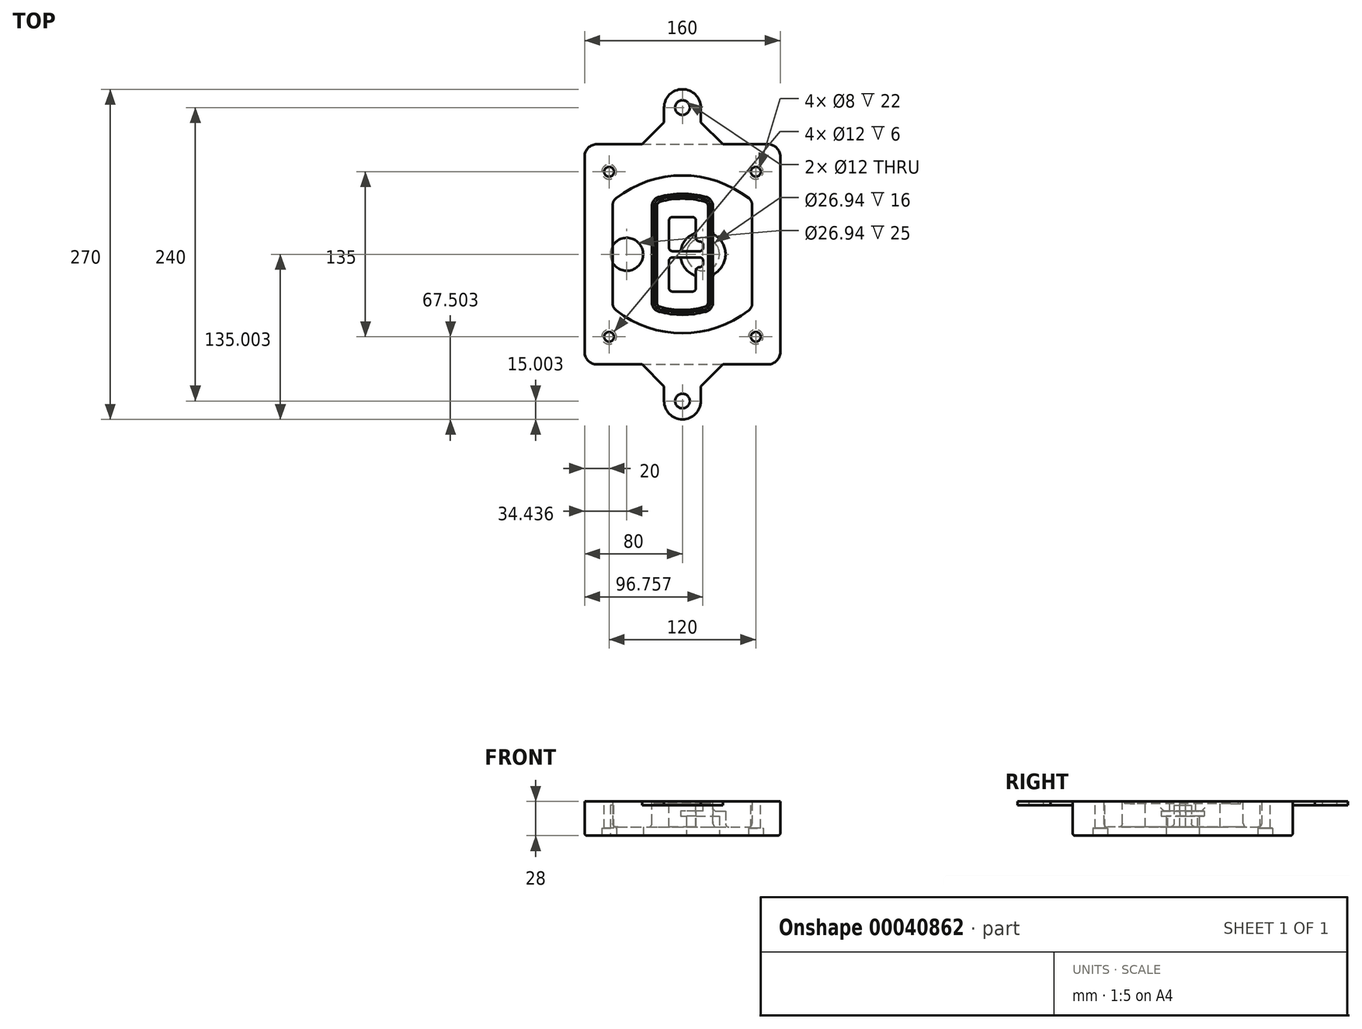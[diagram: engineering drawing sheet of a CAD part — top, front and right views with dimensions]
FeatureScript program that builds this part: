
annotation { "Feature Type Name" : "Feature", "Feature Type Description" : "" }
export const myFeature = defineFeature(function(context is Context, id is Id, definition is map)
    precondition{}
    {
        {
            var Q0;
            Q0=qCreatedBy(makeId("Top.planeOp"),FACE);
            var sketch = newSketch(context, id + "F0", { "sketchPlane" : qUnion([Q0])});
            skPoint(sketch, "E0.rect.middle", {"position": v(0, 0) * mm});
            skLineSegment(sketch, "E1.bottom", {"start": v(24.05, 28.38) * mm, "end": v(164.05, 28.38) * mm});
            skLineSegment(sketch, "E1.top", {"start": v(24.05, 208.38) * mm, "end": v(164.05, 208.38) * mm});
            skLineSegment(sketch, "E1.left", {"start": v(14.05, 38.38) * mm, "end": v(14.05, 198.38) * mm});
            skLineSegment(sketch, "E1.right", {"start": v(174.05, 38.38) * mm, "end": v(174.05, 198.38) * mm});
            skLineSegment(sketch, "E2", {"start": v(14.05, 208.38) * mm, "end": v(174.05, 28.38) * mm, "construction": true});
            skLineSegment(sketch, "E3", {"start": v(174.05, 208.38) * mm, "end": v(14.05, 28.38) * mm, "construction": true});
            skCircle(sketch, "E4", {"center": v(34.05, 185.88) * mm, "radius": 4 * mm});
            skCircle(sketch, "E5", {"center": v(154.05, 185.88) * mm, "radius": 4 * mm});
            skCircle(sketch, "E6", {"center": v(154.05, 50.88) * mm, "radius": 4 * mm});
            skCircle(sketch, "E7", {"center": v(34.05, 50.88) * mm, "radius": 4 * mm});
            skLineSegment(sketch, "E8", {"start": v(34.05, 185.88) * mm, "end": v(154.05, 185.88) * mm, "construction": true});
            skLineSegment(sketch, "E9", {"start": v(154.05, 185.88) * mm, "end": v(154.05, 50.88) * mm, "construction": true});
            skLineSegment(sketch, "E10", {"start": v(154.05, 50.88) * mm, "end": v(34.05, 50.88) * mm, "construction": true});
            skLineSegment(sketch, "E11", {"start": v(34.05, 50.88) * mm, "end": v(34.05, 185.88) * mm, "construction": true});
            skLineSegment(sketch, "E12", {"start": v(34.05, 158.68) * mm, "end": v(34.05, 78.09) * mm});
            skLineSegment(sketch, "E13", {"start": v(154.05, 158.68) * mm, "end": v(154.05, 78.09) * mm});
            skArc(sketch, "E14", {"start": v(150.2, 166.56) * mm, "mid": v(94.05, 185.88) * mm, "end": v(37.9, 166.56) * mm});
            skArc(sketch, "E15", {"start": v(37.9, 70.2) * mm, "mid": v(94.05, 50.88) * mm, "end": v(150.2, 70.2) * mm});
            skLineSegment(sketch, "E16", {"start": v(34.05, 118.38) * mm, "end": v(154.05, 118.38) * mm, "construction": true});
            skPoint(sketch, "E17.visualSharp", {"position": v(34.05, 73.38) * mm});
            skArc(sketch, "E17.filletArc", {"start": v(34.05, 78.09) * mm, "mid": v(35.06, 73.7) * mm, "end": v(37.9, 70.2) * mm});
            skPoint(sketch, "E18.visualSharp", {"position": v(34.05, 163.38) * mm});
            skArc(sketch, "E18.filletArc", {"start": v(37.9, 166.56) * mm, "mid": v(35.06, 163.06) * mm, "end": v(34.05, 158.68) * mm});
            skPoint(sketch, "E19.visualSharp", {"position": v(154.05, 163.38) * mm});
            skArc(sketch, "E19.filletArc", {"start": v(154.05, 158.68) * mm, "mid": v(153.04, 163.06) * mm, "end": v(150.2, 166.56) * mm});
            skPoint(sketch, "E20.visualSharp", {"position": v(154.05, 73.38) * mm});
            skArc(sketch, "E20.filletArc", {"start": v(150.2, 70.2) * mm, "mid": v(153.04, 73.7) * mm, "end": v(154.05, 78.09) * mm});
            skPoint(sketch, "E21.visualSharp", {"position": v(14.05, 208.38) * mm});
            skArc(sketch, "E21.filletArc", {"start": v(24.05, 208.38) * mm, "mid": v(16.98, 205.45) * mm, "end": v(14.05, 198.38) * mm});
            skPoint(sketch, "E22.visualSharp", {"position": v(174.05, 208.38) * mm});
            skArc(sketch, "E22.filletArc", {"start": v(174.05, 198.38) * mm, "mid": v(171.12, 205.45) * mm, "end": v(164.05, 208.38) * mm});
            skPoint(sketch, "E23.visualSharp", {"position": v(174.05, 28.38) * mm});
            skArc(sketch, "E23.filletArc", {"start": v(164.05, 28.38) * mm, "mid": v(171.12, 31.31) * mm, "end": v(174.05, 38.38) * mm});
            skPoint(sketch, "E24.visualSharp", {"position": v(14.05, 28.38) * mm});
            skArc(sketch, "E24.filletArc", {"start": v(14.05, 38.38) * mm, "mid": v(16.98, 31.31) * mm, "end": v(24.05, 28.38) * mm});
            skArc(sketch, "E25.0", {"start": v(151.05, 158.68) * mm, "mid": v(150.34, 161.75) * mm, "end": v(148.36, 164.2) * mm});
            skLineSegment(sketch, "E25.1", {"start": v(151.05, 158.68) * mm, "end": v(151.05, 78.09) * mm});
            skArc(sketch, "E25.2", {"start": v(148.36, 72.57) * mm, "mid": v(150.34, 75.02) * mm, "end": v(151.05, 78.09) * mm});
            skArc(sketch, "E25.3", {"start": v(39.74, 72.57) * mm, "mid": v(94.05, 53.88) * mm, "end": v(148.36, 72.57) * mm});
            skArc(sketch, "E25.4", {"start": v(37.05, 78.09) * mm, "mid": v(37.76, 75.02) * mm, "end": v(39.74, 72.57) * mm});
            skArc(sketch, "E25.5", {"start": v(148.36, 164.2) * mm, "mid": v(94.05, 182.88) * mm, "end": v(39.74, 164.2) * mm});
            skLineSegment(sketch, "E25.6", {"start": v(37.05, 158.68) * mm, "end": v(37.05, 78.09) * mm});
            skArc(sketch, "E25.7", {"start": v(39.74, 164.2) * mm, "mid": v(37.76, 161.75) * mm, "end": v(37.05, 158.68) * mm});
            skArc(sketch, "E26.0", {"start": v(35.43, 169.71) * mm, "mid": v(31.47, 164.82) * mm, "end": v(30.05, 158.68) * mm});
            skArc(sketch, "E26.1", {"start": v(152.67, 169.71) * mm, "mid": v(94.05, 189.88) * mm, "end": v(35.43, 169.71) * mm});
            skArc(sketch, "E26.2", {"start": v(158.05, 158.68) * mm, "mid": v(156.63, 164.82) * mm, "end": v(152.67, 169.71) * mm});
            skLineSegment(sketch, "E26.3", {"start": v(158.05, 158.68) * mm, "end": v(158.05, 78.09) * mm});
            skArc(sketch, "E26.4", {"start": v(152.67, 67.05) * mm, "mid": v(156.63, 71.95) * mm, "end": v(158.05, 78.09) * mm});
            skLineSegment(sketch, "E26.5", {"start": v(30.05, 158.68) * mm, "end": v(30.05, 78.09) * mm});
            skArc(sketch, "E26.6", {"start": v(35.43, 67.05) * mm, "mid": v(94.05, 46.88) * mm, "end": v(152.67, 67.05) * mm});
            skArc(sketch, "E26.7", {"start": v(30.05, 78.09) * mm, "mid": v(31.47, 71.95) * mm, "end": v(35.43, 67.05) * mm});
            skSolve(sketch);
        }
        {
            var Q0;
            Q0=makeQuery(id+"F0.imprint","IMPRINT",FACE,{"disambiguationData":[TD([[makeQuery(id+"F0.imprint","IMPRINT",EDGE,{"derivedFrom":sQuery(id+"F0.wireOp",EDGE,"E1.bottom")}),1.0]])]});
            var Q1;
            Q1=makeQuery(id+"F0.imprint","IMPRINT",FACE,{"disambiguationData":[TD([[makeQuery(id+"F0.imprint","IMPRINT",EDGE,{"derivedFrom":sQuery(id+"F0.wireOp",EDGE,"E12")}),1.0]])]});
            var Q2;
            Q2=makeQuery(id+"F0.imprint","IMPRINT",FACE,{"disambiguationData":[TD([[makeQuery(id+"F0.imprint","IMPRINT",EDGE,{"derivedFrom":sQuery(id+"F0.wireOp",EDGE,"E25.0")}),1.0]])]});
            var Q3;
            Q3=makeQuery(id+"F0.imprint","IMPRINT",FACE,{"disambiguationData":[TD([[makeQuery(id+"F0.imprint","IMPRINT",EDGE,{"derivedFrom":sQuery(id+"F0.wireOp",EDGE,"E12")}),-1.0]])]});
            extrude(context, id + "F1", {"entities" : qUnion([Q0, Q1, Q2, Q3]), "oppositeDirection" : true, "depth" : 25 * mm});
        }
        {
            var Q0;
            Q0=makeQuery(id+"F0.imprint","IMPRINT",FACE,{"disambiguationData":[TD([[makeQuery(id+"F0.imprint","IMPRINT",EDGE,{"derivedFrom":sQuery(id+"F0.wireOp",EDGE,"E12")}),1.0]])]});
            extrude(context, id + "F2", {"entities" : qUnion([Q0]), "operationType" : NewBodyOperationType.ADD, "depth" : 3 * mm});
        }
        {
            var Q0;
            Q0=makeQuery(id+"F0.imprint","IMPRINT",FACE,{"disambiguationData":[TD([[makeQuery(id+"F0.imprint","IMPRINT",EDGE,{"derivedFrom":sQuery(id+"F0.wireOp",EDGE,"E25.0")}),1.0]])]});
            extrude(context, id + "F3", {"entities" : qUnion([Q0]), "operationType" : NewBodyOperationType.REMOVE, "oppositeDirection" : true, "depth" : 18 * mm});
        }
        {
            var Q0;
            Q0=makeQuery(id+"F2.opExtrude","CAP_FACE",FACE,{"disambiguationData":[OSD([sQuery(id+"F0.wireOp",EDGE,"E12"),sQuery(id+"F0.wireOp",EDGE,"E13"),sQuery(id+"F0.wireOp",EDGE,"E14"),sQuery(id+"F0.wireOp",EDGE,"E15"),sQuery(id+"F0.wireOp",EDGE,"E17.filletArc"),sQuery(id+"F0.wireOp",EDGE,"E18.filletArc"),sQuery(id+"F0.wireOp",EDGE,"E19.filletArc"),sQuery(id+"F0.wireOp",EDGE,"E20.filletArc"),sQuery(id+"F0.wireOp",EDGE,"E25.0"),sQuery(id+"F0.wireOp",EDGE,"E25.1"),sQuery(id+"F0.wireOp",EDGE,"E25.2"),sQuery(id+"F0.wireOp",EDGE,"E25.3"),sQuery(id+"F0.wireOp",EDGE,"E25.4"),sQuery(id+"F0.wireOp",EDGE,"E25.5"),sQuery(id+"F0.wireOp",EDGE,"E25.6"),sQuery(id+"F0.wireOp",EDGE,"E25.7")])],"isStart":false});
            var sketch = newSketch(context, id + "F4", { "sketchPlane" : qUnion([Q0])});
            skArc(sketch, "E27.0", {"start": v(74.97, 71.41) * mm, "mid": v(94.05, 68.88) * mm, "end": v(113.13, 71.41) * mm});
            skArc(sketch, "E28.0", {"start": v(113.13, 165.35) * mm, "mid": v(94.05, 167.88) * mm, "end": v(74.97, 165.35) * mm});
            skLineSegment(sketch, "E29", {"start": v(69.05, 157.63) * mm, "end": v(69.05, 79.14) * mm});
            skLineSegment(sketch, "E30", {"start": v(119.05, 157.63) * mm, "end": v(119.05, 79.14) * mm});
            skLineSegment(sketch, "E31", {"start": v(69.05, 163.48) * mm, "end": v(119.05, 163.48) * mm, "construction": true});
            skLineSegment(sketch, "E32", {"start": v(69.05, 73.28) * mm, "end": v(119.05, 73.28) * mm, "construction": true});
            skPoint(sketch, "E33.visualSharp", {"position": v(69.05, 163.48) * mm});
            skArc(sketch, "E33.filletArc", {"start": v(74.97, 165.35) * mm, "mid": v(70.7, 162.5) * mm, "end": v(69.05, 157.63) * mm});
            skPoint(sketch, "E34.visualSharp", {"position": v(119.05, 163.48) * mm});
            skArc(sketch, "E34.filletArc", {"start": v(119.05, 157.63) * mm, "mid": v(117.4, 162.5) * mm, "end": v(113.13, 165.35) * mm});
            skPoint(sketch, "E35.visualSharp", {"position": v(119.05, 73.28) * mm});
            skArc(sketch, "E35.filletArc", {"start": v(113.13, 71.41) * mm, "mid": v(117.4, 74.27) * mm, "end": v(119.05, 79.14) * mm});
            skPoint(sketch, "E36.visualSharp", {"position": v(69.05, 73.28) * mm});
            skArc(sketch, "E36.filletArc", {"start": v(69.05, 79.14) * mm, "mid": v(70.7, 74.27) * mm, "end": v(74.97, 71.41) * mm});
            skArc(sketch, "E37.0", {"start": v(148.36, 164.2) * mm, "mid": v(94.05, 182.88) * mm, "end": v(39.74, 164.2) * mm});
            skArc(sketch, "E37.1", {"start": v(39.74, 164.2) * mm, "mid": v(37.76, 161.75) * mm, "end": v(37.05, 158.68) * mm});
            skLineSegment(sketch, "E37.2", {"start": v(37.05, 158.68) * mm, "end": v(37.05, 78.09) * mm});
            skArc(sketch, "E37.3", {"start": v(37.05, 78.09) * mm, "mid": v(37.76, 75.02) * mm, "end": v(39.74, 72.57) * mm});
            skArc(sketch, "E37.4", {"start": v(39.74, 72.57) * mm, "mid": v(94.05, 53.88) * mm, "end": v(148.36, 72.57) * mm});
            skArc(sketch, "E37.5", {"start": v(148.36, 72.57) * mm, "mid": v(150.34, 75.02) * mm, "end": v(151.05, 78.09) * mm});
            skLineSegment(sketch, "E37.6", {"start": v(151.05, 158.68) * mm, "end": v(151.05, 78.09) * mm});
            skArc(sketch, "E37.7", {"start": v(151.05, 158.68) * mm, "mid": v(150.34, 161.75) * mm, "end": v(148.36, 164.2) * mm});
            skLineSegment(sketch, "E38.0", {"start": v(117.05, 157.63) * mm, "end": v(117.05, 79.14) * mm});
            skArc(sketch, "E38.1", {"start": v(112.61, 73.34) * mm, "mid": v(115.81, 75.49) * mm, "end": v(117.05, 79.14) * mm});
            skArc(sketch, "E38.2", {"start": v(75.49, 73.34) * mm, "mid": v(94.05, 70.88) * mm, "end": v(112.61, 73.34) * mm});
            skArc(sketch, "E38.3", {"start": v(71.05, 79.14) * mm, "mid": v(72.29, 75.49) * mm, "end": v(75.49, 73.34) * mm});
            skLineSegment(sketch, "E38.4", {"start": v(71.05, 157.63) * mm, "end": v(71.05, 79.14) * mm});
            skArc(sketch, "E38.5", {"start": v(117.05, 157.63) * mm, "mid": v(115.81, 161.28) * mm, "end": v(112.61, 163.42) * mm});
            skArc(sketch, "E38.6", {"start": v(75.49, 163.42) * mm, "mid": v(72.29, 161.28) * mm, "end": v(71.05, 157.63) * mm});
            skArc(sketch, "E38.7", {"start": v(112.61, 163.42) * mm, "mid": v(94.05, 165.88) * mm, "end": v(75.49, 163.42) * mm});
            skArc(sketch, "E39.0", {"start": v(115.05, 157.63) * mm, "mid": v(114.23, 160.06) * mm, "end": v(112.1, 161.5) * mm});
            skLineSegment(sketch, "E39.1", {"start": v(115.05, 157.63) * mm, "end": v(115.05, 79.14) * mm});
            skArc(sketch, "E39.2", {"start": v(112.1, 75.27) * mm, "mid": v(114.23, 76.7) * mm, "end": v(115.05, 79.14) * mm});
            skArc(sketch, "E39.3", {"start": v(76, 75.27) * mm, "mid": v(94.05, 72.88) * mm, "end": v(112.1, 75.27) * mm});
            skArc(sketch, "E39.4", {"start": v(73.05, 79.14) * mm, "mid": v(73.87, 76.7) * mm, "end": v(76, 75.27) * mm});
            skArc(sketch, "E39.5", {"start": v(112.1, 161.5) * mm, "mid": v(94.05, 163.88) * mm, "end": v(76, 161.5) * mm});
            skLineSegment(sketch, "E39.6", {"start": v(73.05, 157.63) * mm, "end": v(73.05, 79.14) * mm});
            skArc(sketch, "E39.7", {"start": v(76, 161.5) * mm, "mid": v(73.87, 160.06) * mm, "end": v(73.05, 157.63) * mm});
            skLineSegment(sketch, "E40", {"start": v(69.05, 118.38) * mm, "end": v(119.05, 118.38) * mm, "construction": true});
            skLineSegment(sketch, "E41", {"start": v(83.05, 123.88) * mm, "end": v(83.05, 145.88) * mm});
            skLineSegment(sketch, "E42", {"start": v(86.05, 148.88) * mm, "end": v(102.05, 148.88) * mm});
            skLineSegment(sketch, "E43", {"start": v(105.05, 145.88) * mm, "end": v(105.05, 131.88) * mm});
            skLineSegment(sketch, "E44", {"start": v(108.05, 128.88) * mm, "end": v(108.05, 128.88) * mm});
            skLineSegment(sketch, "E45", {"start": v(111.05, 125.88) * mm, "end": v(111.05, 123.88) * mm});
            skLineSegment(sketch, "E46", {"start": v(108.05, 120.88) * mm, "end": v(86.05, 120.88) * mm});
            skPoint(sketch, "E47.visualSharp", {"position": v(83.05, 148.88) * mm});
            skArc(sketch, "E47.filletArc", {"start": v(86.05, 148.88) * mm, "mid": v(83.93, 148) * mm, "end": v(83.05, 145.88) * mm});
            skPoint(sketch, "E48.visualSharp", {"position": v(105.05, 148.88) * mm});
            skArc(sketch, "E48.filletArc", {"start": v(105.05, 145.88) * mm, "mid": v(104.17, 148) * mm, "end": v(102.05, 148.88) * mm});
            skPoint(sketch, "E49.visualSharp", {"position": v(105.05, 128.88) * mm});
            skArc(sketch, "E49.filletArc", {"start": v(105.05, 131.88) * mm, "mid": v(105.93, 129.76) * mm, "end": v(108.05, 128.88) * mm});
            skPoint(sketch, "E50.visualSharp", {"position": v(111.05, 128.88) * mm});
            skArc(sketch, "E50.filletArc", {"start": v(111.05, 125.88) * mm, "mid": v(110.17, 128) * mm, "end": v(108.05, 128.88) * mm});
            skPoint(sketch, "E51.visualSharp", {"position": v(111.05, 120.88) * mm});
            skArc(sketch, "E51.filletArc", {"start": v(108.05, 120.88) * mm, "mid": v(110.17, 121.76) * mm, "end": v(111.05, 123.88) * mm});
            skPoint(sketch, "E52.visualSharp", {"position": v(83.05, 120.88) * mm});
            skArc(sketch, "E52.filletArc", {"start": v(83.05, 123.88) * mm, "mid": v(83.93, 121.76) * mm, "end": v(86.05, 120.88) * mm});
            skLineSegment(sketch, "E53.0.MirrorCS", {"start": v(108.05, 115.88) * mm, "end": v(86.05, 115.88) * mm});
            skArc(sketch, "E54.0.MirrorCS", {"start": v(83.05, 112.88) * mm, "mid": v(83.93, 115) * mm, "end": v(86.05, 115.88) * mm});
            skLineSegment(sketch, "E55.0.MirrorCS", {"start": v(83.05, 112.88) * mm, "end": v(83.05, 90.88) * mm});
            skArc(sketch, "E56.0.MirrorCS", {"start": v(86.05, 87.88) * mm, "mid": v(83.93, 88.76) * mm, "end": v(83.05, 90.88) * mm});
            skLineSegment(sketch, "E57.0.MirrorCS", {"start": v(86.05, 87.88) * mm, "end": v(102.05, 87.88) * mm});
            skArc(sketch, "E58.0.MirrorCS", {"start": v(105.05, 90.88) * mm, "mid": v(104.17, 88.76) * mm, "end": v(102.05, 87.88) * mm});
            skLineSegment(sketch, "E59.0.MirrorCS", {"start": v(105.05, 90.88) * mm, "end": v(105.05, 104.88) * mm});
            skArc(sketch, "E60.0.MirrorCS", {"start": v(105.05, 104.88) * mm, "mid": v(105.93, 107) * mm, "end": v(108.05, 107.88) * mm});
            skArc(sketch, "E61.0.MirrorCS", {"start": v(111.05, 110.88) * mm, "mid": v(110.17, 108.76) * mm, "end": v(108.05, 107.88) * mm});
            skLineSegment(sketch, "E62.0.MirrorCS", {"start": v(111.05, 110.88) * mm, "end": v(111.05, 112.88) * mm});
            skArc(sketch, "E63.0.MirrorCS", {"start": v(108.05, 115.88) * mm, "mid": v(110.17, 115) * mm, "end": v(111.05, 112.88) * mm});
            skSolve(sketch);
        }
        {
            var Q0;
            Q0=makeQuery(id+"F4.imprint","IMPRINT",FACE,{"disambiguationData":[TD([[makeQuery(id+"F4.imprint","IMPRINT",EDGE,{"derivedFrom":sQuery(id+"F4.wireOp",EDGE,"E27.0")}),1.0]])]});
            var Q1;
            Q1=makeQuery(id+"F4.imprint","IMPRINT",FACE,{"disambiguationData":[TD([[makeQuery(id+"F4.imprint","IMPRINT",EDGE,{"derivedFrom":sQuery(id+"F4.wireOp",EDGE,"E38.0")}),-1.0]])]});
            var Q2;
            Q2=makeQuery(id+"F4.imprint","IMPRINT",FACE,{"disambiguationData":[TD([[makeQuery(id+"F4.imprint","IMPRINT",EDGE,{"derivedFrom":sQuery(id+"F4.wireOp",EDGE,"E39.0")}),1.0]])]});
            extrude(context, id + "F5", {"entities" : qUnion([Q0, Q1, Q2]), "operationType" : NewBodyOperationType.ADD, "endBound" : BoundingType.UP_TO_NEXT, "oppositeDirection" : true, "depth" : 25 * mm});
        }
        {
            var Q0;
            Q0=makeQuery(id+"F4.imprint","IMPRINT",FACE,{"disambiguationData":[TD([[makeQuery(id+"F4.imprint","IMPRINT",EDGE,{"derivedFrom":sQuery(id+"F4.wireOp",EDGE,"E38.0")}),-1.0]])]});
            extrude(context, id + "F6", {"entities" : qUnion([Q0]), "operationType" : NewBodyOperationType.REMOVE, "oppositeDirection" : true, "depth" : 2 * mm});
        }
        {
            var Q0;
            Q0=makeQuery(id+"F1.opExtrude","CAP_FACE",FACE,{"disambiguationData":[OSD([sQuery(id+"F0.wireOp",EDGE,"E1.bottom"),sQuery(id+"F0.wireOp",EDGE,"E1.top"),sQuery(id+"F0.wireOp",EDGE,"E1.left"),sQuery(id+"F0.wireOp",EDGE,"E1.right"),sQuery(id+"F0.wireOp",EDGE,"E4"),sQuery(id+"F0.wireOp",EDGE,"E5"),sQuery(id+"F0.wireOp",EDGE,"E6"),sQuery(id+"F0.wireOp",EDGE,"E7"),sQuery(id+"F0.wireOp",EDGE,"E21.filletArc"),sQuery(id+"F0.wireOp",EDGE,"E22.filletArc"),sQuery(id+"F0.wireOp",EDGE,"E23.filletArc"),sQuery(id+"F0.wireOp",EDGE,"E24.filletArc")])],"isStart":false});
            var sketch = newSketch(context, id + "F7", { "sketchPlane" : qUnion([Q0])});
            skCircle(sketch, "E64", {"center": v(110.8, -118.38) * mm, "radius": 13.47 * mm});
            skCircle(sketch, "E65", {"center": v(48.49, -118.38) * mm, "radius": 13.47 * mm});
            skLineSegment(sketch, "E66", {"start": v(174.05, -118.38) * mm, "end": v(14.05, -118.38) * mm});
            skCircle(sketch, "E67", {"center": v(110.8, -118.38) * mm, "radius": 18.47 * mm});
            skCircle(sketch, "E68", {"center": v(154.05, -185.88) * mm, "radius": 6 * mm});
            skCircle(sketch, "E69", {"center": v(34.05, -185.88) * mm, "radius": 6 * mm});
            skCircle(sketch, "E70", {"center": v(34.05, -50.88) * mm, "radius": 6 * mm});
            skCircle(sketch, "E71", {"center": v(154.05, -50.88) * mm, "radius": 6 * mm});
            skSolve(sketch);
        }
        {
            var Q0;
            {var subQ1=sQuery(id+"F7.wireOp",EDGE,"E66");var subQ4=sQuery(id+"F7.wireOp",EDGE,"E64");var subQ6=makeQuery(id+"F7.imprint","INTERSECT",VERTEX,{"disambiguationData":[OD(0.0)],"derivedFrom":[subQ4,subQ1]});Q0=makeQuery(id+"F7.imprint","IMPRINT",FACE,{"disambiguationData":[TD([[makeQuery(id+"F7.imprint","IMPRINT",EDGE,{"disambiguationData":[TD([[subQ6,-1.0]])],"derivedFrom":subQ4}),-1.0]])]});}
            var Q1;
            {var subQ0=sQuery(id+"F7.wireOp",EDGE,"E66");var subQ1=sQuery(id+"F7.wireOp",EDGE,"E64");var subQ3=makeQuery(id+"F7.imprint","INTERSECT",VERTEX,{"disambiguationData":[OD(0.0)],"derivedFrom":[subQ1,subQ0]});Q1=makeQuery(id+"F7.imprint","IMPRINT",FACE,{"disambiguationData":[TD([[makeQuery(id+"F7.imprint","IMPRINT",EDGE,{"disambiguationData":[TD([[subQ3,-1.0]])],"derivedFrom":subQ1}),1.0]])]});}
            var Q2;
            {var subQ0=sQuery(id+"F7.wireOp",EDGE,"E66");var subQ1=sQuery(id+"F7.wireOp",EDGE,"E64");var subQ3=makeQuery(id+"F7.imprint","INTERSECT",VERTEX,{"disambiguationData":[OD(0.0)],"derivedFrom":[subQ1,subQ0]});Q2=makeQuery(id+"F7.imprint","IMPRINT",FACE,{"disambiguationData":[TD([[makeQuery(id+"F7.imprint","IMPRINT",EDGE,{"disambiguationData":[TD([[subQ3,1.0]])],"derivedFrom":subQ1}),1.0]])]});}
            var Q3;
            {var subQ1=sQuery(id+"F7.wireOp",EDGE,"E66");var subQ4=sQuery(id+"F7.wireOp",EDGE,"E64");var subQ6=makeQuery(id+"F7.imprint","INTERSECT",VERTEX,{"disambiguationData":[OD(0.0)],"derivedFrom":[subQ4,subQ1]});Q3=makeQuery(id+"F7.imprint","IMPRINT",FACE,{"disambiguationData":[TD([[makeQuery(id+"F7.imprint","IMPRINT",EDGE,{"disambiguationData":[TD([[subQ6,1.0]])],"derivedFrom":subQ4}),-1.0]])]});}
            extrude(context, id + "F8", {"entities" : qUnion([Q0, Q1, Q2, Q3]), "operationType" : NewBodyOperationType.ADD, "oppositeDirection" : true, "depth" : 20 * mm});
        }
        {
            var Q0;
            {var subQ0=sQuery(id+"F7.wireOp",EDGE,"E66");var subQ1=sQuery(id+"F7.wireOp",EDGE,"E64");var subQ3=makeQuery(id+"F7.imprint","INTERSECT",VERTEX,{"disambiguationData":[OD(0.0)],"derivedFrom":[subQ1,subQ0]});Q0=makeQuery(id+"F7.imprint","IMPRINT",FACE,{"disambiguationData":[TD([[makeQuery(id+"F7.imprint","IMPRINT",EDGE,{"disambiguationData":[TD([[subQ3,-1.0]])],"derivedFrom":subQ1}),1.0]])]});}
            var Q1;
            {var subQ0=sQuery(id+"F7.wireOp",EDGE,"E66");var subQ1=sQuery(id+"F7.wireOp",EDGE,"E64");var subQ3=makeQuery(id+"F7.imprint","INTERSECT",VERTEX,{"disambiguationData":[OD(0.0)],"derivedFrom":[subQ1,subQ0]});Q1=makeQuery(id+"F7.imprint","IMPRINT",FACE,{"disambiguationData":[TD([[makeQuery(id+"F7.imprint","IMPRINT",EDGE,{"disambiguationData":[TD([[subQ3,1.0]])],"derivedFrom":subQ1}),1.0]])]});}
            extrude(context, id + "F9", {"entities" : qUnion([Q0, Q1]), "operationType" : NewBodyOperationType.REMOVE, "oppositeDirection" : true, "depth" : 16 * mm});
        }
        {
            var Q0;
            {var subQ0=sQuery(id+"F7.wireOp",EDGE,"E66");var subQ1=sQuery(id+"F7.wireOp",EDGE,"E65");var subQ3=makeQuery(id+"F7.imprint","INTERSECT",VERTEX,{"disambiguationData":[OD(0.0)],"derivedFrom":[subQ1,subQ0]});Q0=makeQuery(id+"F7.imprint","IMPRINT",FACE,{"disambiguationData":[TD([[makeQuery(id+"F7.imprint","IMPRINT",EDGE,{"disambiguationData":[TD([[subQ3,-1.0]])],"derivedFrom":subQ1}),1.0]])]});}
            var Q1;
            {var subQ0=sQuery(id+"F7.wireOp",EDGE,"E66");var subQ1=sQuery(id+"F7.wireOp",EDGE,"E65");var subQ3=makeQuery(id+"F7.imprint","INTERSECT",VERTEX,{"disambiguationData":[OD(0.0)],"derivedFrom":[subQ1,subQ0]});Q1=makeQuery(id+"F7.imprint","IMPRINT",FACE,{"disambiguationData":[TD([[makeQuery(id+"F7.imprint","IMPRINT",EDGE,{"disambiguationData":[TD([[subQ3,1.0]])],"derivedFrom":subQ1}),1.0]])]});}
            extrude(context, id + "F10", {"entities" : qUnion([Q0, Q1]), "operationType" : NewBodyOperationType.REMOVE, "oppositeDirection" : true, "depth" : 25 * mm});
        }
        {
            var Q0;
            Q0=makeQuery(id+"F7.imprint","IMPRINT",FACE,{"disambiguationData":[TD([[makeQuery(id+"F7.imprint","IMPRINT",EDGE,{"derivedFrom":sQuery(id+"F7.wireOp",EDGE,"E68")}),1.0]])]});
            var Q1;
            Q1=makeQuery(id+"F7.imprint","IMPRINT",FACE,{"disambiguationData":[TD([[makeQuery(id+"F7.imprint","IMPRINT",EDGE,{"derivedFrom":makeQuery(id+"F1.opExtrude","CAP_EDGE",EDGE,{"disambiguationData":[OSD([sQuery(id+"F0.wireOp",EDGE,"E5")])],"isStart":false})}),-1.0]])]});
            var Q2;
            Q2=makeQuery(id+"F7.imprint","IMPRINT",FACE,{"disambiguationData":[TD([[makeQuery(id+"F7.imprint","IMPRINT",EDGE,{"derivedFrom":sQuery(id+"F7.wireOp",EDGE,"E69")}),1.0]])]});
            var Q3;
            Q3=makeQuery(id+"F7.imprint","IMPRINT",FACE,{"disambiguationData":[TD([[makeQuery(id+"F7.imprint","IMPRINT",EDGE,{"derivedFrom":makeQuery(id+"F1.opExtrude","CAP_EDGE",EDGE,{"disambiguationData":[OSD([sQuery(id+"F0.wireOp",EDGE,"E4")])],"isStart":false})}),-1.0]])]});
            var Q4;
            Q4=makeQuery(id+"F7.imprint","IMPRINT",FACE,{"disambiguationData":[TD([[makeQuery(id+"F7.imprint","IMPRINT",EDGE,{"derivedFrom":sQuery(id+"F7.wireOp",EDGE,"E70")}),1.0]])]});
            var Q5;
            Q5=makeQuery(id+"F7.imprint","IMPRINT",FACE,{"disambiguationData":[TD([[makeQuery(id+"F7.imprint","IMPRINT",EDGE,{"derivedFrom":makeQuery(id+"F1.opExtrude","CAP_EDGE",EDGE,{"disambiguationData":[OSD([sQuery(id+"F0.wireOp",EDGE,"E7")])],"isStart":false})}),-1.0]])]});
            var Q6;
            Q6=makeQuery(id+"F7.imprint","IMPRINT",FACE,{"disambiguationData":[TD([[makeQuery(id+"F7.imprint","IMPRINT",EDGE,{"derivedFrom":sQuery(id+"F7.wireOp",EDGE,"E71")}),1.0]])]});
            var Q7;
            Q7=makeQuery(id+"F7.imprint","IMPRINT",FACE,{"disambiguationData":[TD([[makeQuery(id+"F7.imprint","IMPRINT",EDGE,{"derivedFrom":makeQuery(id+"F1.opExtrude","CAP_EDGE",EDGE,{"disambiguationData":[OSD([sQuery(id+"F0.wireOp",EDGE,"E6")])],"isStart":false})}),-1.0]])]});
            extrude(context, id + "F11", {"entities" : qUnion([Q0, Q1, Q2, Q3, Q4, Q5, Q6, Q7]), "operationType" : NewBodyOperationType.REMOVE, "oppositeDirection" : true, "depth" : 6 * mm});
        }
        {
            var Q0;
            Q0=makeQuery(id+"F9.boolean.opBoolean","COPY",FACE,{"derivedFrom":makeQuery(id+"F9.opExtrude","CAP_FACE",FACE,{"disambiguationData":[OSD([sQuery(id+"F7.wireOp",EDGE,"E64")])],"isStart":false})});
            var sketch = newSketch(context, id + "F12", { "sketchPlane" : qUnion([Q0])});
            skArc(sketch, "E72.0", {"start": v(105.05, -100.83) * mm, "mid": v(96.62, -106.56) * mm, "end": v(92.5, -115.88) * mm});
            skArc(sketch, "E72.1", {"start": v(92.5, -120.88) * mm, "mid": v(96.62, -130.2) * mm, "end": v(105.05, -135.93) * mm});
            skLineSegment(sketch, "E73", {"start": v(92.5, -120.88) * mm, "end": v(108.05, -120.88) * mm});
            skLineSegment(sketch, "E74.0", {"start": v(108.05, -115.88) * mm, "end": v(92.5, -115.88) * mm});
            skArc(sketch, "E74.1", {"start": v(108.05, -115.88) * mm, "mid": v(110.17, -115) * mm, "end": v(111.05, -112.88) * mm});
            skLineSegment(sketch, "E74.2", {"start": v(111.05, -110.88) * mm, "end": v(111.05, -112.88) * mm});
            skArc(sketch, "E74.3", {"start": v(111.05, -110.88) * mm, "mid": v(110.17, -108.76) * mm, "end": v(108.05, -107.88) * mm});
            skArc(sketch, "E74.4", {"start": v(105.05, -104.88) * mm, "mid": v(105.93, -107) * mm, "end": v(108.05, -107.88) * mm});
            skLineSegment(sketch, "E74.5", {"start": v(105.05, -100.83) * mm, "end": v(105.05, -104.88) * mm});
            skLineSegment(sketch, "E74.7", {"start": v(108.05, -120.88) * mm, "end": v(92.5, -120.88) * mm});
            skArc(sketch, "E74.8", {"start": v(108.05, -120.88) * mm, "mid": v(110.17, -121.76) * mm, "end": v(111.05, -123.88) * mm});
            skLineSegment(sketch, "E74.9", {"start": v(111.05, -125.88) * mm, "end": v(111.05, -123.88) * mm});
            skArc(sketch, "E74.10", {"start": v(111.05, -125.88) * mm, "mid": v(110.17, -128) * mm, "end": v(108.05, -128.88) * mm});
            skArc(sketch, "E74.11", {"start": v(105.05, -131.88) * mm, "mid": v(105.93, -129.76) * mm, "end": v(108.05, -128.88) * mm});
            skLineSegment(sketch, "E74.12", {"start": v(105.05, -135.93) * mm, "end": v(105.05, -131.88) * mm});
            skPoint(sketch, "E75.orphan", {"position": v(105.05, -145.88) * mm});
            skPoint(sketch, "E76.orphan", {"position": v(86.05, -120.88) * mm});
            skPoint(sketch, "E77.orphan", {"position": v(86.05, -115.88) * mm});
            skPoint(sketch, "E78.orphan", {"position": v(105.05, -90.88) * mm});
            skSolve(sketch);
        }
        {
            var Q0;
            {var subQ7=sQuery(id+"F12.wireOp",EDGE,"E72.0");var subQ14=sQuery(id+"F12.wireOp",EDGE,"E72.1");var subQ16=sQuery(id+"F12.wireOp",EDGE,"E74.1");var subQ18=sQuery(id+"F12.wireOp",EDGE,"E74.8");Q0=qUnion([makeQuery(id+"F12.imprint","IMPRINT",FACE,{"disambiguationData":[TD([[makeQuery(id+"F12.imprint","IMPRINT",EDGE,{"derivedFrom":subQ7}),1.0]])]}),makeQuery(id+"F12.imprint","IMPRINT",FACE,{"disambiguationData":[TD([[makeQuery(id+"F12.imprint","IMPRINT",EDGE,{"derivedFrom":subQ14}),1.0]])]}),makeQuery(id+"F12.imprint","IMPRINT",FACE,{"disambiguationData":[TD([[makeQuery(id+"F12.imprint","IMPRINT",EDGE,{"derivedFrom":subQ16}),1.0]])]}),makeQuery(id+"F12.imprint","IMPRINT",FACE,{"disambiguationData":[TD([[makeQuery(id+"F12.imprint","IMPRINT",EDGE,{"derivedFrom":subQ18}),-1.0]])]})]);}
            var Q1;
            Q1=makeQuery(id+"F5.boolean.opBoolean","SPLIT",FACE,{"disambiguationData":[TD([makeQuery(id+"F5.opExtrude","SWEPT_FACE",FACE,{"disambiguationData":[OSD([sQuery(id+"F4.wireOp",EDGE,"E41")])]})])],"derivedFrom":makeQuery(id+"F3.boolean.opBoolean","COPY",FACE,{"derivedFrom":makeQuery(id+"F3.opExtrude","CAP_FACE",FACE,{"disambiguationData":[OSD([sQuery(id+"F0.wireOp",EDGE,"E25.0"),sQuery(id+"F0.wireOp",EDGE,"E25.1"),sQuery(id+"F0.wireOp",EDGE,"E25.2"),sQuery(id+"F0.wireOp",EDGE,"E25.3"),sQuery(id+"F0.wireOp",EDGE,"E25.4"),sQuery(id+"F0.wireOp",EDGE,"E25.5"),sQuery(id+"F0.wireOp",EDGE,"E25.6"),sQuery(id+"F0.wireOp",EDGE,"E25.7")])],"isStart":false})})});
            extrude(context, id + "F13", {"entities" : qUnion([Q0]), "operationType" : NewBodyOperationType.REMOVE, "endBound" : BoundingType.UP_TO_SURFACE, "endBoundEntityFace" : qUnion([Q1]), "depth" : 25 * mm});
        }
        {
            var Q0;
            Q0=makeQuery(id+"F3.boolean.opBoolean","COPY",EDGE,{"derivedFrom":makeQuery(id+"F3.opExtrude","CAP_EDGE",EDGE,{"disambiguationData":[OSD([sQuery(id+"F0.wireOp",EDGE,"E25.6")])],"isStart":false})});
            var Q1;
            Q1=makeQuery(id+"F8.boolean.opBoolean","INTERSECT",EDGE,{"derivedFrom":[makeQuery(id+"F5.opExtrude","SWEPT_FACE",FACE,{"disambiguationData":[OSD([sQuery(id+"F4.wireOp",EDGE,"E30")])]}),makeQuery(id+"F8.opExtrude","CAP_FACE",FACE,{"disambiguationData":[OSD([sQuery(id+"F7.wireOp",EDGE,"E67")])],"isStart":false})]});
            var Q2;
            Q2=makeQuery(id+"F8.boolean.opBoolean","INTERSECT",EDGE,{"disambiguationData":[OD(1.0)],"derivedFrom":[makeQuery(id+"F5.opExtrude","SWEPT_FACE",FACE,{"disambiguationData":[OSD([sQuery(id+"F4.wireOp",EDGE,"E30")])]}),makeQuery(id+"F8.opExtrude","SWEPT_FACE",FACE,{"disambiguationData":[OSD([sQuery(id+"F7.wireOp",EDGE,"E67")])]})]});
            var Q3;
            {var subQ0=sQuery(id+"F4.wireOp",EDGE,"E30");Q3=makeQuery(id+"F8.boolean.opBoolean","SPLIT",EDGE,{"disambiguationData":[TD([makeQuery(id+"F5.opExtrude","SWEPT_FACE",FACE,{"disambiguationData":[OSD([sQuery(id+"F4.wireOp",EDGE,"E35.filletArc")])]})])],"derivedFrom":makeQuery(id+"F5.opExtrude","CAP_EDGE",EDGE,{"disambiguationData":[OSD([subQ0])],"isStart":false})});}
            var Q4;
            {var subQ0=sQuery(id+"F0.wireOp",EDGE,"E25.7");var subQ1=sQuery(id+"F0.wireOp",EDGE,"E25.1");var subQ2=sQuery(id+"F0.wireOp",EDGE,"E25.6");var subQ3=sQuery(id+"F0.wireOp",EDGE,"E25.5");var subQ4=sQuery(id+"F0.wireOp",EDGE,"E25.4");var subQ5=sQuery(id+"F0.wireOp",EDGE,"E25.0");var subQ6=sQuery(id+"F0.wireOp",EDGE,"E25.2");var subQ7=sQuery(id+"F0.wireOp",EDGE,"E25.3");Q4=makeQuery(id+"F8.boolean.opBoolean","INTERSECT",EDGE,{"derivedFrom":[makeQuery(id+"F5.boolean.opBoolean","SPLIT",FACE,{"disambiguationData":[TD([makeQuery(id+"F2.opExtrude","SWEPT_FACE",FACE,{"disambiguationData":[OSD([subQ5])]})])],"derivedFrom":makeQuery(id+"F3.boolean.opBoolean","COPY",FACE,{"derivedFrom":makeQuery(id+"F3.opExtrude","CAP_FACE",FACE,{"disambiguationData":[OSD([subQ5,subQ1,subQ6,subQ7,subQ4,subQ3,subQ2,subQ0])],"isStart":false})})}),makeQuery(id+"F8.opExtrude","SWEPT_FACE",FACE,{"disambiguationData":[OSD([sQuery(id+"F7.wireOp",EDGE,"E67")])]})]});}
            var Q5;
            Q5=makeQuery(id+"F8.boolean.opBoolean","INTERSECT",EDGE,{"disambiguationData":[OD(0.0)],"derivedFrom":[makeQuery(id+"F5.opExtrude","SWEPT_FACE",FACE,{"disambiguationData":[OSD([sQuery(id+"F4.wireOp",EDGE,"E30")])]}),makeQuery(id+"F8.opExtrude","SWEPT_FACE",FACE,{"disambiguationData":[OSD([sQuery(id+"F7.wireOp",EDGE,"E67")])]})]});
            fillet(context, id + "F14", {"entities" : qUnion([Q0, Q1, Q2, Q3, Q4, Q5]), "radius" : 3 * mm, "tangentPropagation" : true, "allowEdgeOverflow" : false});
        }
        {
            var Q0;
            Q0=makeQuery(id+"F1.opExtrude","CAP_EDGE",EDGE,{"disambiguationData":[OSD([sQuery(id+"F0.wireOp",EDGE,"E1.bottom")])],"isStart":false});
            fillet(context, id + "F15", {"entities" : qUnion([Q0]), "radius" : 2 * mm, "tangentPropagation" : true, "allowEdgeOverflow" : false});
        }
        {
            var Q0;
            {var subQ0=sQuery(id+"F0.wireOp",EDGE,"E1.bottom");var subQ1=sQuery(id+"F0.wireOp",EDGE,"E1.top");var subQ2=sQuery(id+"F0.wireOp",EDGE,"E1.left");var subQ3=sQuery(id+"F0.wireOp",EDGE,"E1.right");var subQ4=sQuery(id+"F0.wireOp",EDGE,"E4");var subQ5=sQuery(id+"F0.wireOp",EDGE,"E5");var subQ6=sQuery(id+"F0.wireOp",EDGE,"E6");var subQ7=sQuery(id+"F0.wireOp",EDGE,"E7");var subQ8=sQuery(id+"F0.wireOp",EDGE,"E21.filletArc");var subQ9=sQuery(id+"F0.wireOp",EDGE,"E22.filletArc");var subQ10=sQuery(id+"F0.wireOp",EDGE,"E23.filletArc");var subQ11=sQuery(id+"F0.wireOp",EDGE,"E24.filletArc");Q0=makeQuery(id+"F2.boolean.opBoolean","SPLIT",FACE,{"disambiguationData":[TD([makeQuery(id+"F1.opExtrude","SWEPT_FACE",FACE,{"disambiguationData":[OSD([subQ0])]})])],"derivedFrom":makeQuery(id+"F1.opExtrude","CAP_FACE",FACE,{"disambiguationData":[OSD([subQ0,subQ1,subQ2,subQ3,subQ4,subQ5,subQ6,subQ7,subQ8,subQ9,subQ10,subQ11])],"isStart":true})});}
            var sketch = newSketch(context, id + "F16", { "sketchPlane" : qUnion([Q0])});
            skLineSegment(sketch, "E79", {"start": v(94.05, 208.38) * mm, "end": v(94.05, 238.38) * mm, "construction": true});
            skLineSegment(sketch, "E80", {"start": v(79.05, 238.38) * mm, "end": v(79.05, 226.38) * mm});
            skLineSegment(sketch, "E81", {"start": v(79.05, 226.38) * mm, "end": v(61.05, 208.38) * mm});
            skCircle(sketch, "E82", {"center": v(94.05, 238.38) * mm, "radius": 6 * mm});
            skLineSegment(sketch, "E83", {"start": v(109.05, 238.38) * mm, "end": v(109.05, 226.38) * mm});
            skLineSegment(sketch, "E84", {"start": v(109.05, 226.38) * mm, "end": v(127.05, 208.38) * mm});
            skArc(sketch, "E85", {"start": v(109.05, 238.38) * mm, "mid": v(94.05, 253.38) * mm, "end": v(79.05, 238.38) * mm});
            skLineSegment(sketch, "E86", {"start": v(14.05, 118.38) * mm, "end": v(174.05, 118.38) * mm, "construction": true});
            skLineSegment(sketch, "E87.MirrorCS", {"start": v(109.05, 10.38) * mm, "end": v(127.05, 28.38) * mm});
            skLineSegment(sketch, "E88.MirrorCS", {"start": v(109.05, -1.62) * mm, "end": v(109.05, 10.38) * mm});
            skArc(sketch, "E89.MirrorCS", {"start": v(109.05, -1.62) * mm, "mid": v(94.05, -16.62) * mm, "end": v(79.05, -1.62) * mm});
            skLineSegment(sketch, "E90.MirrorCS", {"start": v(79.05, -1.62) * mm, "end": v(79.05, 10.38) * mm});
            skLineSegment(sketch, "E91.MirrorCS", {"start": v(79.05, 10.38) * mm, "end": v(61.05, 28.38) * mm});
            skCircle(sketch, "E92.MirrorC", {"center": v(94.05, -1.62) * mm, "radius": 6 * mm});
            skLineSegment(sketch, "E93.MirrorCS", {"start": v(94.05, 28.38) * mm, "end": v(94.05, -1.62) * mm, "construction": true});
            skSolve(sketch);
        }
        {
            var Q0;
            Q0=makeQuery(id+"F16.imprint","IMPRINT",FACE,{"disambiguationData":[TD([[makeQuery(id+"F16.imprint","IMPRINT",EDGE,{"derivedFrom":makeQuery(id+"F1.opExtrude","CAP_EDGE",EDGE,{"disambiguationData":[OSD([sQuery(id+"F0.wireOp",EDGE,"E1.left")])],"isStart":true})}),-1.0]])]});
            var Q1;
            {var subQ1=sQuery(id+"F16.wireOp",EDGE,"E87.MirrorCS");Q1=makeQuery(id+"F16.imprint","IMPRINT",FACE,{"disambiguationData":[TD([[makeQuery(id+"F16.imprint","IMPRINT",EDGE,{"derivedFrom":subQ1}),1.0]])]});}
            var Q2;
            Q2=makeQuery(id+"F16.imprint","IMPRINT",FACE,{"disambiguationData":[TD([[makeQuery(id+"F16.imprint","IMPRINT",EDGE,{"derivedFrom":sQuery(id+"F16.wireOp",EDGE,"E80")}),1.0]])]});
            var Q3;
            Q3=makeQuery(id+"F2.opExtrude","CAP_FACE",FACE,{"disambiguationData":[OSD([sQuery(id+"F0.wireOp",EDGE,"E12"),sQuery(id+"F0.wireOp",EDGE,"E13"),sQuery(id+"F0.wireOp",EDGE,"E14"),sQuery(id+"F0.wireOp",EDGE,"E15"),sQuery(id+"F0.wireOp",EDGE,"E17.filletArc"),sQuery(id+"F0.wireOp",EDGE,"E18.filletArc"),sQuery(id+"F0.wireOp",EDGE,"E19.filletArc"),sQuery(id+"F0.wireOp",EDGE,"E20.filletArc"),sQuery(id+"F0.wireOp",EDGE,"E25.0"),sQuery(id+"F0.wireOp",EDGE,"E25.1"),sQuery(id+"F0.wireOp",EDGE,"E25.2"),sQuery(id+"F0.wireOp",EDGE,"E25.3"),sQuery(id+"F0.wireOp",EDGE,"E25.4"),sQuery(id+"F0.wireOp",EDGE,"E25.5"),sQuery(id+"F0.wireOp",EDGE,"E25.6"),sQuery(id+"F0.wireOp",EDGE,"E25.7")])],"isStart":false});
            extrude(context, id + "F17", {"entities" : qUnion([Q0, Q1, Q2]), "operationType" : NewBodyOperationType.ADD, "endBound" : BoundingType.UP_TO_SURFACE, "endBoundEntityFace" : qUnion([Q3]), "depth" : 25 * mm});
        }
    });
